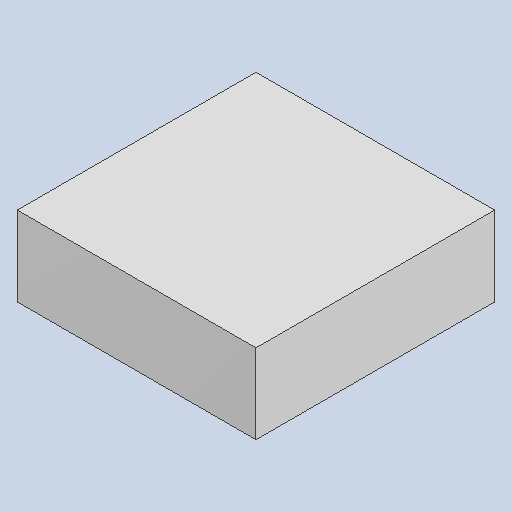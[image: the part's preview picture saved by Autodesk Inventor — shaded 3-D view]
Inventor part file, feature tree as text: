
AUTODESK INVENTOR PART (.ipt)
format: ipt  version: 2023.4 (Build 274418000, 418)  size: 79,872 bytes
history: native  units: mm
features: extrude x1
ambient origin geometry x8: Origin, YZ Plane, XZ Plane, XY Plane, X Axis, Y Axis, Z Axis, Center Point
bodies: Solid1 (feature_tree)
feature tree (1):
  extrude  "Extruded_58"  [1 undecoded]
note: 1 required parameter value undecoded (feature->parameter linkage not recoverable at this tier; creation-order binding heuristic only, values carry confidence <= 0.55)
